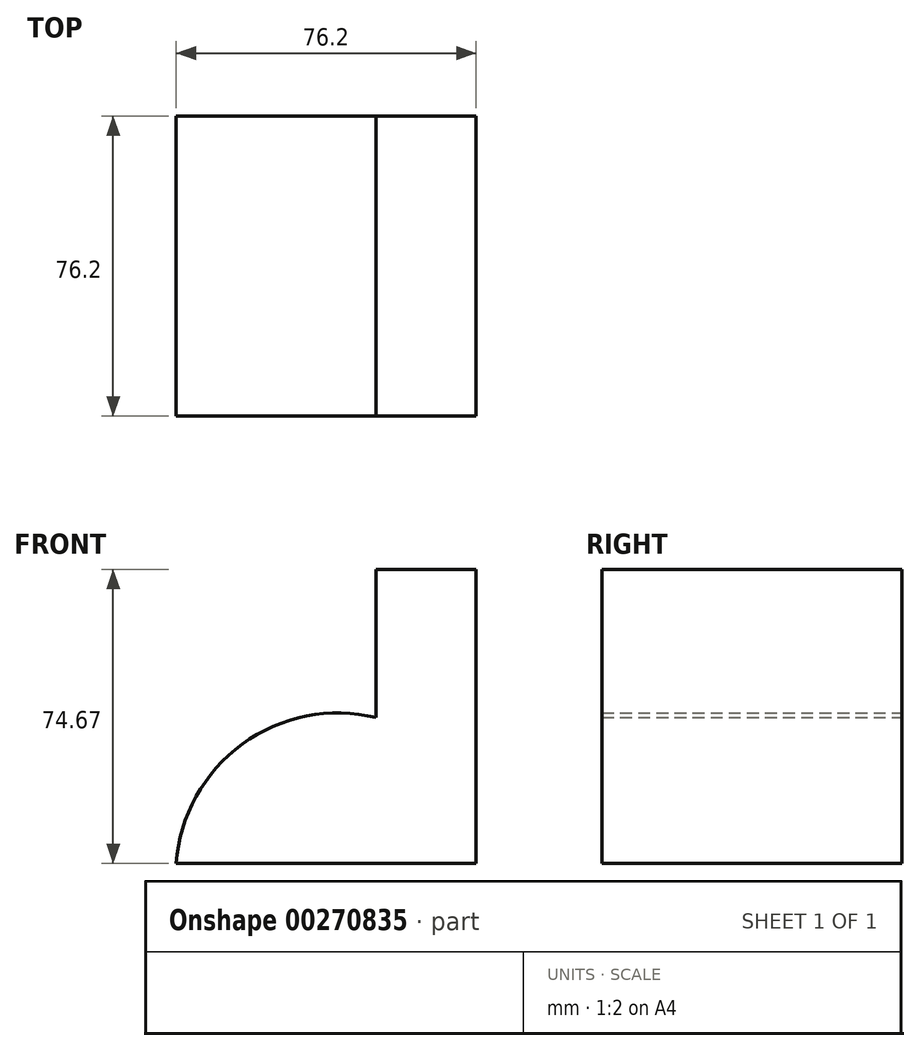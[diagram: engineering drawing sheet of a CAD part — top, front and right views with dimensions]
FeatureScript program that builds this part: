
annotation { "Feature Type Name" : "Feature", "Feature Type Description" : "" }
export const myFeature = defineFeature(function(context is Context, id is Id, definition is map)
    precondition{}
    {
        {
            var Q0;
            Q0=qCreatedBy(makeId("Front.planeOp"),FACE);
            var sketch = newSketch(context, id + "F0", { "sketchPlane" : qUnion([Q0])});
            skLineSegment(sketch, "E0", {"start": v(0, -1.53) * mm, "end": v(0, 74.67) * mm});
            skLineSegment(sketch, "E1", {"start": v(0, 0) * mm, "end": v(-76.2, 0) * mm});
            skLineSegment(sketch, "E2", {"start": v(0, 74.67) * mm, "end": v(-25.4, 74.67) * mm});
            skLineSegment(sketch, "E3", {"start": v(-25.4, 74.67) * mm, "end": v(-25.4, 37.05) * mm});
            skArc(sketch, "E4", {"start": v(-25.4, 37.05) * mm, "mid": v(-59.4, 30.3) * mm, "end": v(-76.2, 0) * mm});
            skSolve(sketch);
        }
        {
            var Q0;
            Q0 = qSketchRegion(id + "F0", true);
            extrude(context, id + "F1", {"entities" : qUnion([Q0]), "depth" : 76.2 * mm});
        }
    });
